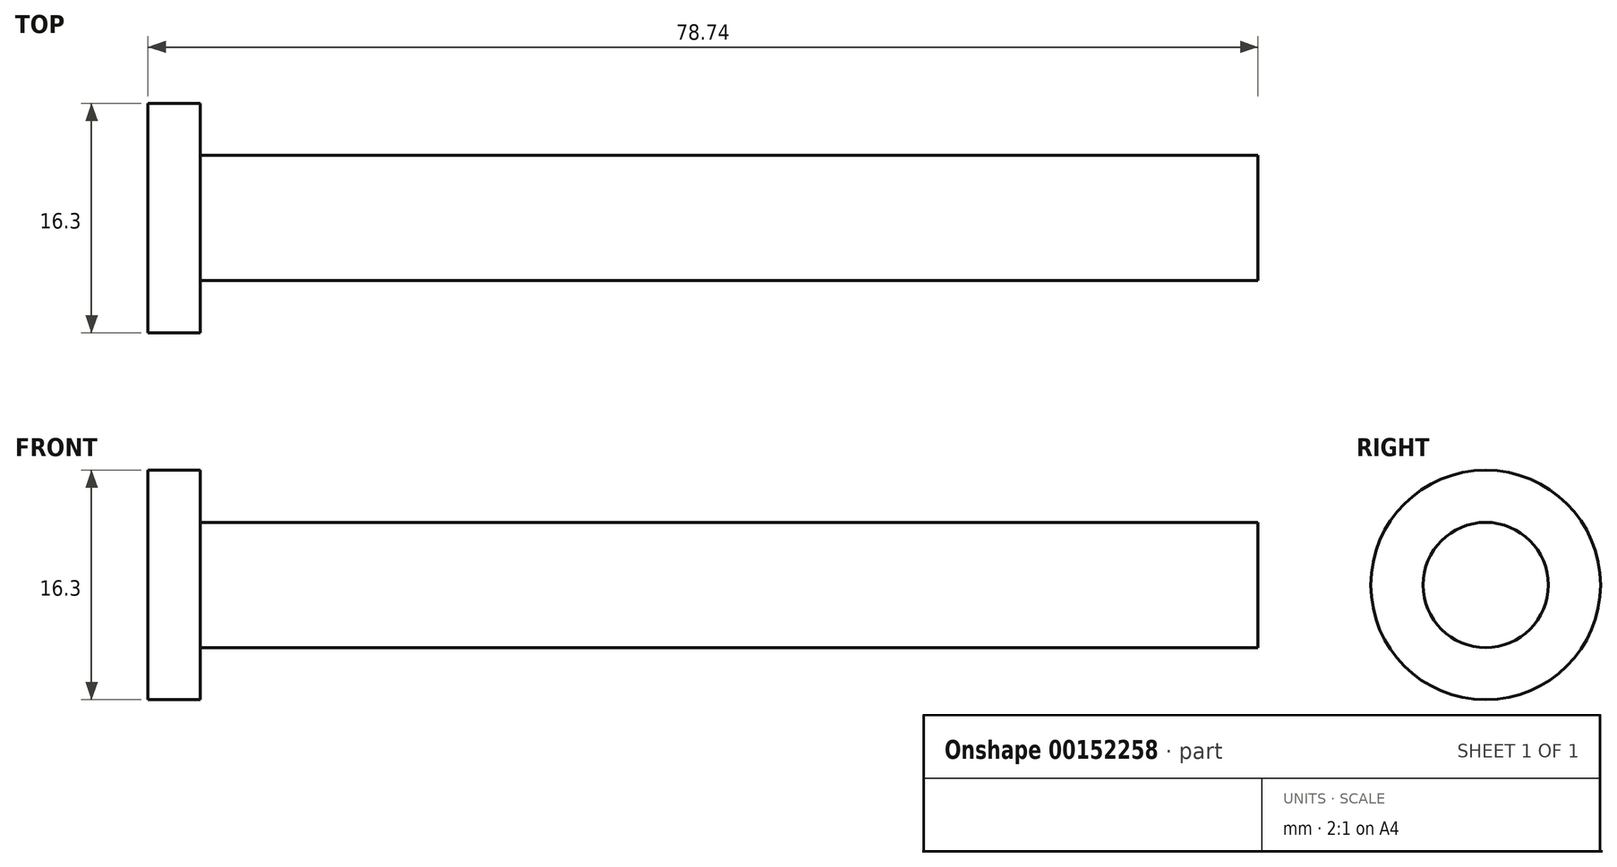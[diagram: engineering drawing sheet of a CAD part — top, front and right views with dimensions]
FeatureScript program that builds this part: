
annotation { "Feature Type Name" : "Feature", "Feature Type Description" : "" }
export const myFeature = defineFeature(function(context is Context, id is Id, definition is map)
    precondition{}
    {
        {
            var Q0;
            Q0=qCreatedBy(makeId("Front.planeOp"),FACE);
            var sketch = newSketch(context, id + "F0", { "sketchPlane" : qUnion([Q0])});
            skLineSegment(sketch, "E0", {"start": v(0, 0) * mm, "end": v(0, 8.15) * mm});
            skLineSegment(sketch, "E1", {"start": v(0, 8.15) * mm, "end": v(3.7, 8.15) * mm});
            skLineSegment(sketch, "E2", {"start": v(3.7, 8.15) * mm, "end": v(3.7, 4.44) * mm});
            skLineSegment(sketch, "E3", {"start": v(3.7, 4.44) * mm, "end": v(78.74, 4.45) * mm});
            skLineSegment(sketch, "E4", {"start": v(78.74, 4.45) * mm, "end": v(78.74, 0) * mm});
            skLineSegment(sketch, "E5", {"start": v(78.74, 0) * mm, "end": v(0, 0) * mm});
            skSolve(sketch);
        }
        {
            var Q0;
            Q0 = qSketchRegion(id + "F0", true);
            var Q1;
            Q1=sQuery(id+"F0.wireOp",EDGE,"E5");
            revolve(context, id + "F1", {"entities" : qUnion([Q0]), "axis" : qUnion([Q1]), "revolveType" : RevolveType.FULL});
        }
    });
